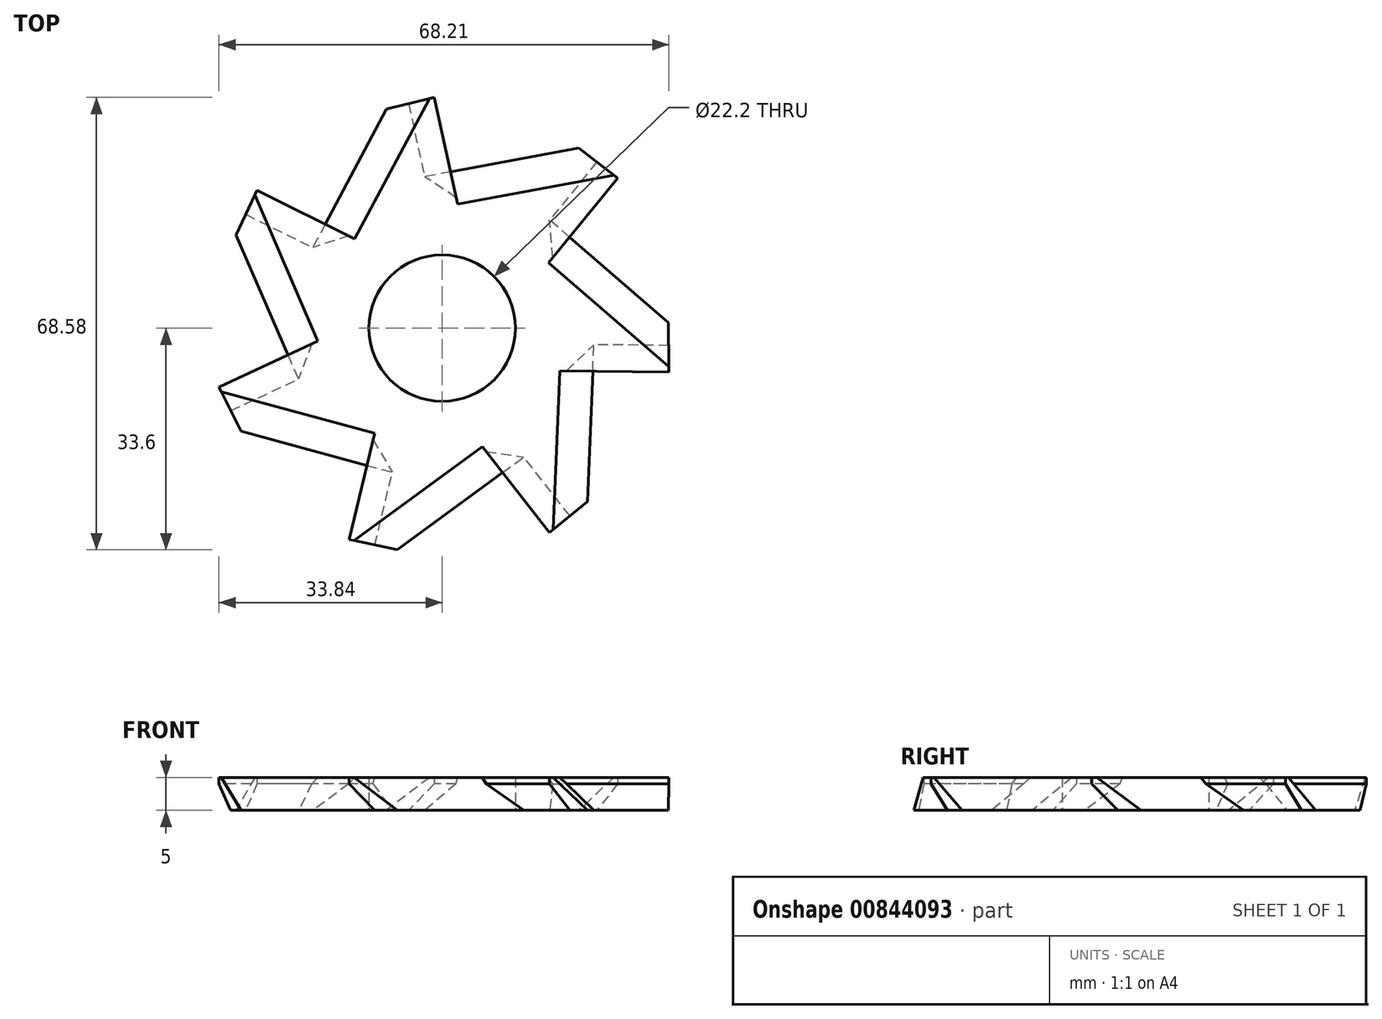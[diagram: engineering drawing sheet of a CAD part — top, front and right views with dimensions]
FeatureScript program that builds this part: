
annotation { "Feature Type Name" : "Feature", "Feature Type Description" : "" }
export const myFeature = defineFeature(function(context is Context, id is Id, definition is map)
    precondition{}
    {
        {
            var Q0;
            Q0=qCreatedBy(makeId("Top.planeOp"),FACE);
            var sketch = newSketch(context, id + "F0", { "sketchPlane" : qUnion([Q0])});
            skCircle(sketch, "E0", {"center": v(0, 0) * mm, "radius": 11.1 * mm});
            skCircle(sketch, "E1", {"center": v(0, 0) * mm, "radius": 15.3 * mm});
            skCircle(sketch, "E2", {"center": v(0, 0) * mm, "radius": 35 * mm, "construction": true});
            skLineSegment(sketch, "E3", {"start": v(-9.6, 11.92) * mm, "end": v(-7.41, 27.17) * mm});
            skLineSegment(sketch, "E4", {"start": v(-7.41, 27.17) * mm, "end": v(15.43, 31.42) * mm});
            skLineSegment(sketch, "E5", {"start": v(15.43, 31.42) * mm, "end": v(26.6, 22.74) * mm});
            skLineSegment(sketch, "E6", {"start": v(26.6, 22.74) * mm, "end": v(13.67, 6.89) * mm});
            skLineSegment(sketch, "E7.1.0", {"start": v(-15.3, -0.08) * mm, "end": v(-25.86, 11.15) * mm});
            skLineSegment(sketch, "E7.1.1", {"start": v(-25.86, 11.15) * mm, "end": v(-14.95, 31.65) * mm});
            skLineSegment(sketch, "E7.1.2", {"start": v(-14.95, 31.65) * mm, "end": v(-1.19, 34.98) * mm});
            skLineSegment(sketch, "E7.1.3", {"start": v(-1.19, 34.98) * mm, "end": v(3.14, 14.98) * mm});
            skLineSegment(sketch, "E7.2.0", {"start": v(-9.49, -12.02) * mm, "end": v(-24.84, -13.27) * mm});
            skLineSegment(sketch, "E7.2.1", {"start": v(-24.84, -13.27) * mm, "end": v(-34.06, 8.05) * mm});
            skLineSegment(sketch, "E7.2.2", {"start": v(-34.06, 8.05) * mm, "end": v(-28.09, 20.88) * mm});
            skLineSegment(sketch, "E7.2.3", {"start": v(-28.09, 20.88) * mm, "end": v(-9.76, 11.8) * mm});
            skLineSegment(sketch, "E7.3.0", {"start": v(3.48, -14.9) * mm, "end": v(-5.11, -27.7) * mm});
            skLineSegment(sketch, "E7.3.1", {"start": v(-5.11, -27.7) * mm, "end": v(-27.53, -21.61) * mm});
            skLineSegment(sketch, "E7.3.2", {"start": v(-27.53, -21.61) * mm, "end": v(-33.84, -8.94) * mm});
            skLineSegment(sketch, "E7.3.3", {"start": v(-33.84, -8.94) * mm, "end": v(-15.3, -0.27) * mm});
            skLineSegment(sketch, "E7.4.0", {"start": v(13.83, -6.57) * mm, "end": v(18.47, -21.26) * mm});
            skLineSegment(sketch, "E7.4.1", {"start": v(18.47, -21.26) * mm, "end": v(-0.27, -35) * mm});
            skLineSegment(sketch, "E7.4.2", {"start": v(-0.27, -35) * mm, "end": v(-14.1, -32.03) * mm});
            skLineSegment(sketch, "E7.4.3", {"start": v(-14.1, -32.03) * mm, "end": v(-9.33, -12.14) * mm});
            skLineSegment(sketch, "E7.5.0", {"start": v(13.76, 6.71) * mm, "end": v(28.14, 1.18) * mm});
            skLineSegment(sketch, "E7.5.1", {"start": v(28.14, 1.18) * mm, "end": v(27.2, -22.03) * mm});
            skLineSegment(sketch, "E7.5.2", {"start": v(27.2, -22.03) * mm, "end": v(16.25, -31) * mm});
            skLineSegment(sketch, "E7.5.3", {"start": v(16.25, -31) * mm, "end": v(3.67, -14.86) * mm});
            skLineSegment(sketch, "E7.6.0", {"start": v(3.33, 14.94) * mm, "end": v(16.62, 22.74) * mm});
            skLineSegment(sketch, "E7.6.1", {"start": v(16.62, 22.74) * mm, "end": v(34.18, 7.53) * mm});
            skLineSegment(sketch, "E7.6.2", {"start": v(34.18, 7.53) * mm, "end": v(34.37, -6.63) * mm});
            skLineSegment(sketch, "E7.6.3", {"start": v(34.37, -6.63) * mm, "end": v(13.91, -6.4) * mm});
            skSolve(sketch);
        }
        {
            var Q0;
            Q0=makeQuery(id+"F0.imprint","IMPRINT",FACE,{"disambiguationData":[TD([[makeQuery(id+"F0.imprint","IMPRINT",EDGE,{"derivedFrom":sQuery(id+"F0.wireOp",EDGE,"E0")}),-1.0]])]});
            var Q1;
            {var subQ0=sQuery(id+"F0.wireOp",EDGE,"E7.5.0");Q1=makeQuery(id+"F0.imprint","IMPRINT",FACE,{"disambiguationData":[TD([[makeQuery(id+"F0.imprint","IMPRINT",EDGE,{"derivedFrom":subQ0}),1.0]])]});}
            var Q2;
            {var subQ0=sQuery(id+"F0.wireOp",EDGE,"E7.5.0");Q2=makeQuery(id+"F0.imprint","IMPRINT",FACE,{"disambiguationData":[TD([[makeQuery(id+"F0.imprint","IMPRINT",EDGE,{"derivedFrom":subQ0}),-1.0]])]});}
            var Q3;
            {var subQ5=sQuery(id+"F0.wireOp",EDGE,"E7.4.0");Q3=makeQuery(id+"F0.imprint","IMPRINT",FACE,{"disambiguationData":[TD([[makeQuery(id+"F0.imprint","IMPRINT",EDGE,{"derivedFrom":subQ5}),1.0]])]});}
            var Q4;
            {var subQ0=sQuery(id+"F0.wireOp",EDGE,"E7.4.0");Q4=makeQuery(id+"F0.imprint","IMPRINT",FACE,{"disambiguationData":[TD([[makeQuery(id+"F0.imprint","IMPRINT",EDGE,{"derivedFrom":subQ0}),-1.0]])]});}
            var Q5;
            {var subQ1=sQuery(id+"F0.wireOp",EDGE,"E7.3.0");Q5=makeQuery(id+"F0.imprint","IMPRINT",FACE,{"disambiguationData":[TD([[makeQuery(id+"F0.imprint","IMPRINT",EDGE,{"derivedFrom":subQ1}),1.0]])]});}
            var Q6;
            {var subQ0=sQuery(id+"F0.wireOp",EDGE,"E7.3.0");Q6=makeQuery(id+"F0.imprint","IMPRINT",FACE,{"disambiguationData":[TD([[makeQuery(id+"F0.imprint","IMPRINT",EDGE,{"derivedFrom":subQ0}),-1.0]])]});}
            var Q7;
            {var subQ5=sQuery(id+"F0.wireOp",EDGE,"E7.2.0");Q7=makeQuery(id+"F0.imprint","IMPRINT",FACE,{"disambiguationData":[TD([[makeQuery(id+"F0.imprint","IMPRINT",EDGE,{"derivedFrom":subQ5}),1.0]])]});}
            var Q8;
            {var subQ4=sQuery(id+"F0.wireOp",EDGE,"E7.1.0");Q8=makeQuery(id+"F0.imprint","IMPRINT",FACE,{"disambiguationData":[TD([[makeQuery(id+"F0.imprint","IMPRINT",EDGE,{"derivedFrom":subQ4}),1.0]])]});}
            var Q9;
            {var subQ0=sQuery(id+"F0.wireOp",EDGE,"E7.1.0");Q9=makeQuery(id+"F0.imprint","IMPRINT",FACE,{"disambiguationData":[TD([[makeQuery(id+"F0.imprint","IMPRINT",EDGE,{"derivedFrom":subQ0}),-1.0]])]});}
            var Q10;
            {var subQ5=sQuery(id+"F0.wireOp",EDGE,"E3");Q10=makeQuery(id+"F0.imprint","IMPRINT",FACE,{"disambiguationData":[TD([[makeQuery(id+"F0.imprint","IMPRINT",EDGE,{"derivedFrom":subQ5}),1.0]])]});}
            var Q11;
            {var subQ0=sQuery(id+"F0.wireOp",EDGE,"E3");Q11=makeQuery(id+"F0.imprint","IMPRINT",FACE,{"disambiguationData":[TD([[makeQuery(id+"F0.imprint","IMPRINT",EDGE,{"derivedFrom":subQ0}),-1.0]])]});}
            var Q12;
            {var subQ1=sQuery(id+"F0.wireOp",EDGE,"E5");Q12=makeQuery(id+"F0.imprint","IMPRINT",FACE,{"disambiguationData":[TD([[makeQuery(id+"F0.imprint","IMPRINT",EDGE,{"derivedFrom":subQ1}),-1.0]])]});}
            var Q13;
            {var subQ3=sQuery(id+"F0.wireOp",EDGE,"E7.6.0");Q13=makeQuery(id+"F0.imprint","IMPRINT",FACE,{"disambiguationData":[TD([[makeQuery(id+"F0.imprint","IMPRINT",EDGE,{"derivedFrom":subQ3}),-1.0]])]});}
            var Q14;
            {var subQ0=sQuery(id+"F0.wireOp",EDGE,"E7.2.0");Q14=makeQuery(id+"F0.imprint","IMPRINT",FACE,{"disambiguationData":[TD([[makeQuery(id+"F0.imprint","IMPRINT",EDGE,{"derivedFrom":subQ0}),-1.0]])]});}
            extrude(context, id + "F1", {"entities" : qUnion([Q0, Q1, Q2, Q3, Q4, Q5, Q6, Q7, Q8, Q9, Q10, Q11, Q12, Q13, Q14]), "depth" : 5 * mm, "offsetDistance" : 25 * mm});
        }
        {
            var Q0;
            Q0=makeQuery(id+"F1.opExtrude","CAP_EDGE",EDGE,{"disambiguationData":[OSD([sQuery(id+"F0.wireOp",EDGE,"E7.5.1")])],"isStart":false});
            var Q1;
            Q1=makeQuery(id+"F1.opExtrude","CAP_EDGE",EDGE,{"disambiguationData":[OSD([sQuery(id+"F0.wireOp",EDGE,"E7.4.1")])],"isStart":false});
            var Q2;
            Q2=makeQuery(id+"F1.opExtrude","CAP_EDGE",EDGE,{"disambiguationData":[OSD([sQuery(id+"F0.wireOp",EDGE,"E7.3.1")])],"isStart":false});
            var Q3;
            Q3=makeQuery(id+"F1.opExtrude","CAP_EDGE",EDGE,{"disambiguationData":[OSD([sQuery(id+"F0.wireOp",EDGE,"E7.2.1")])],"isStart":false});
            var Q4;
            Q4=makeQuery(id+"F1.opExtrude","CAP_EDGE",EDGE,{"disambiguationData":[OSD([sQuery(id+"F0.wireOp",EDGE,"E7.1.1")])],"isStart":false});
            var Q5;
            Q5=makeQuery(id+"F1.opExtrude","CAP_EDGE",EDGE,{"disambiguationData":[OSD([sQuery(id+"F0.wireOp",EDGE,"E4")])],"isStart":false});
            var Q6;
            Q6=makeQuery(id+"F1.opExtrude","CAP_EDGE",EDGE,{"disambiguationData":[OSD([sQuery(id+"F0.wireOp",EDGE,"E7.6.1")])],"isStart":false});
            chamfer(context, id + "F2", {"entities" : qUnion([Q0, Q1, Q2, Q3, Q4, Q5, Q6]), "width" : 10 * mm});
        }
        {
            var Q0;
            Q0=makeQuery(id+"F1.opExtrude","CAP_EDGE",EDGE,{"disambiguationData":[OSD([sQuery(id+"F0.wireOp",EDGE,"E6")])],"isStart":true});
            var Q1;
            Q1=makeQuery(id+"F1.opExtrude","CAP_EDGE",EDGE,{"disambiguationData":[OSD([sQuery(id+"F0.wireOp",EDGE,"E7.6.3")])],"isStart":true});
            var Q2;
            Q2=makeQuery(id+"F1.opExtrude","CAP_EDGE",EDGE,{"disambiguationData":[OSD([sQuery(id+"F0.wireOp",EDGE,"E7.5.3")])],"isStart":true});
            var Q3;
            Q3=makeQuery(id+"F1.opExtrude","CAP_EDGE",EDGE,{"disambiguationData":[OSD([sQuery(id+"F0.wireOp",EDGE,"E7.4.3")])],"isStart":true});
            var Q4;
            Q4=makeQuery(id+"F1.opExtrude","CAP_EDGE",EDGE,{"disambiguationData":[OSD([sQuery(id+"F0.wireOp",EDGE,"E7.3.3")])],"isStart":true});
            var Q5;
            Q5=makeQuery(id+"F1.opExtrude","CAP_EDGE",EDGE,{"disambiguationData":[OSD([sQuery(id+"F0.wireOp",EDGE,"E7.2.3")])],"isStart":true});
            var Q6;
            Q6=makeQuery(id+"F1.opExtrude","CAP_EDGE",EDGE,{"disambiguationData":[OSD([sQuery(id+"F0.wireOp",EDGE,"E7.1.3")])],"isStart":true});
            chamfer(context, id + "F3", {"entities" : qUnion([Q0, Q1, Q2, Q3, Q4, Q5, Q6]), "width" : 4 * mm, "tangentPropagation" : true});
        }
    });
